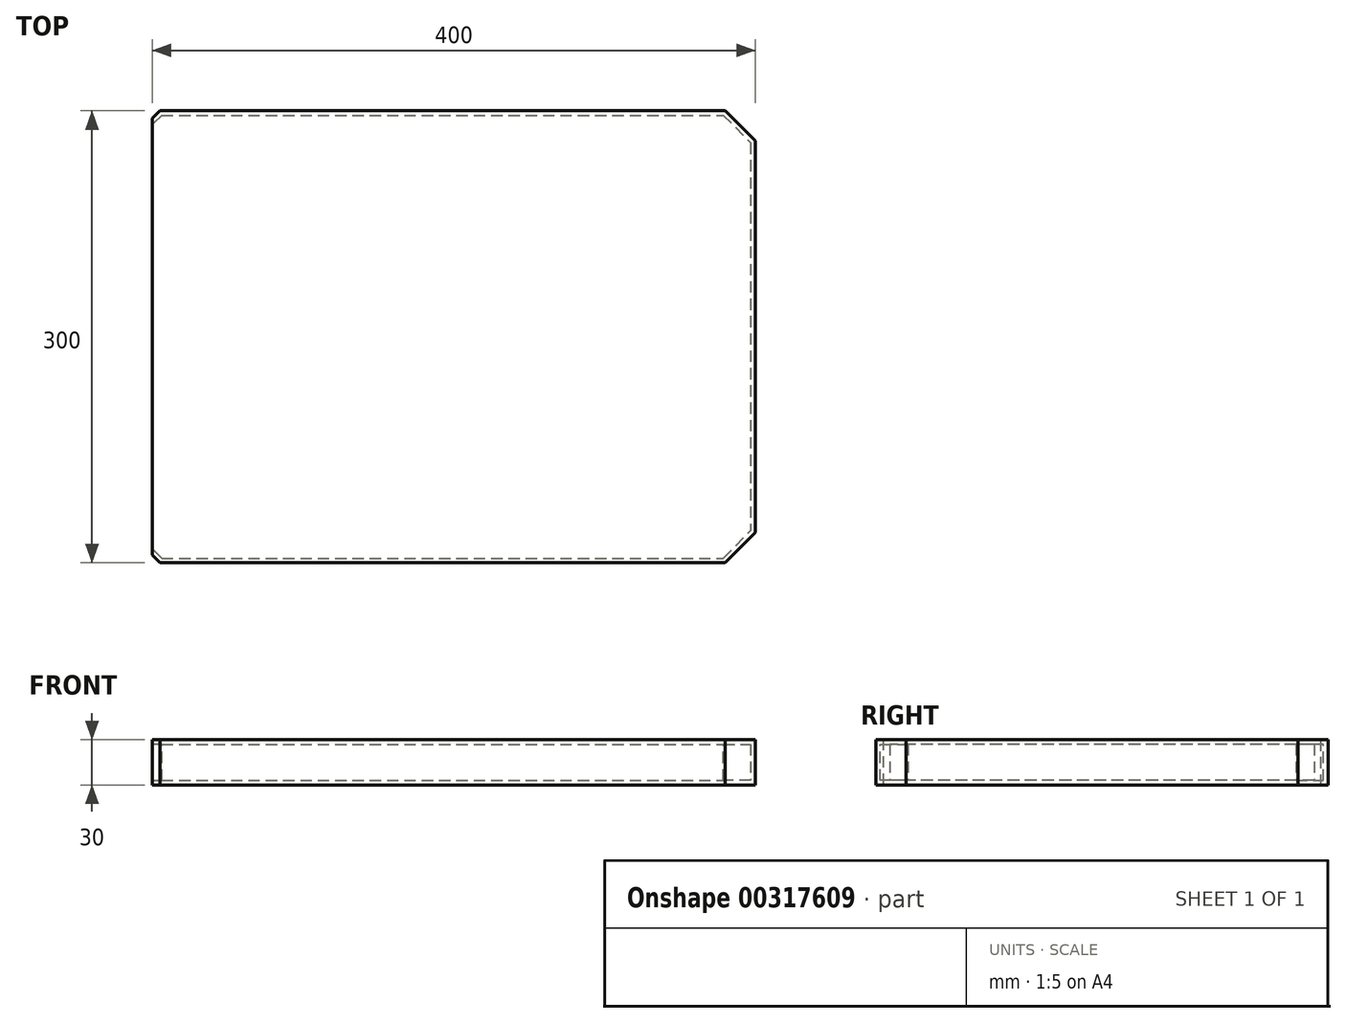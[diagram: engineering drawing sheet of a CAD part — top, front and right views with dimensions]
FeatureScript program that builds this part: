
annotation { "Feature Type Name" : "Feature", "Feature Type Description" : "" }
export const myFeature = defineFeature(function(context is Context, id is Id, definition is map)
    precondition{}
    {
        {
            var Q0;
            Q0=qCreatedBy(makeId("Top.planeOp"),FACE);
            var sketch = newSketch(context, id + "F0", { "sketchPlane" : qUnion([Q0])});
            skLineSegment(sketch, "E0.bottom", {"start": v(-200, 150) * mm, "end": v(200, 150) * mm});
            skLineSegment(sketch, "E0.top", {"start": v(-200, -150) * mm, "end": v(200, -150) * mm});
            skLineSegment(sketch, "E0.left", {"start": v(-200, 150) * mm, "end": v(-200, -150) * mm});
            skLineSegment(sketch, "E0.right", {"start": v(200, 150) * mm, "end": v(200, -150) * mm});
            skSolve(sketch);
        }
        {
            var Q0;
            Q0=makeQuery(id+"F0.imprint","IMPRINT",FACE,{"disambiguationData":[TD([[makeQuery(id+"F0.imprint","IMPRINT",EDGE,{"derivedFrom":sQuery(id+"F0.wireOp",EDGE,"E0.bottom")}),-1.0]])]});
            extrude(context, id + "F1", {"entities" : qUnion([Q0]), "depth" : 30 * mm});
        }
        {
            var Q0;
            Q0=makeQuery(id+"F1.opExtrude","SWEPT_EDGE",EDGE,{"disambiguationData":[OSD([sQuery(id+"F0.wireOp",EDGE,"E0.top"),sQuery(id+"F0.wireOp",EDGE,"E0.right")])]});
            var Q1;
            Q1=makeQuery(id+"F1.opExtrude","SWEPT_EDGE",EDGE,{"disambiguationData":[OSD([sQuery(id+"F0.wireOp",EDGE,"E0.bottom"),sQuery(id+"F0.wireOp",EDGE,"E0.right")])]});
            chamfer(context, id + "F2", {"entities" : qUnion([Q0, Q1]), "width" : 20 * mm, "tangentPropagation" : true});
        }
        {
            var Q0;
            Q0=makeQuery(id+"F1.opExtrude","SWEPT_EDGE",EDGE,{"disambiguationData":[OSD([sQuery(id+"F0.wireOp",EDGE,"E0.top"),sQuery(id+"F0.wireOp",EDGE,"E0.left")])]});
            var Q1;
            Q1=makeQuery(id+"F1.opExtrude","SWEPT_EDGE",EDGE,{"disambiguationData":[OSD([sQuery(id+"F0.wireOp",EDGE,"E0.bottom"),sQuery(id+"F0.wireOp",EDGE,"E0.left")])]});
            chamfer(context, id + "F3", {"entities" : qUnion([Q0, Q1]), "width" : 5 * mm, "tangentPropagation" : true});
        }
        {
            var Q0;
            Q0=makeQuery(id+"F1.opExtrude","SWEPT_FACE",FACE,{"disambiguationData":[OSD([sQuery(id+"F0.wireOp",EDGE,"E0.left")])]});
            shell(context, id + "F4", {"entities" : qUnion([Q0]), "thickness" : 3 * mm});
        }
    });
